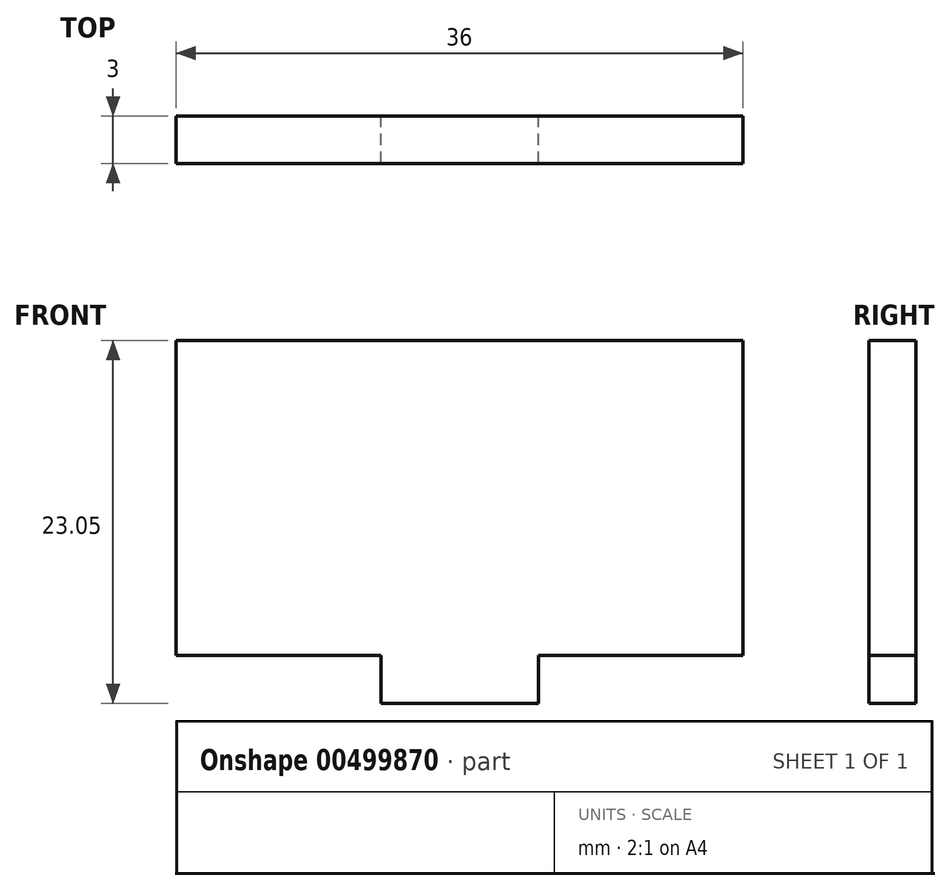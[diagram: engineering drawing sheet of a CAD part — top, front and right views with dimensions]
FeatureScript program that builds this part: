
annotation { "Feature Type Name" : "Feature", "Feature Type Description" : "" }
export const myFeature = defineFeature(function(context is Context, id is Id, definition is map)
    precondition{}
    {
        {
            var Q0;
            Q0=qCreatedBy(makeId("Front.planeOp"),FACE);
            var sketch = newSketch(context, id + "F0", { "sketchPlane" : qUnion([Q0])});
            skLineSegment(sketch, "E0.bottom", {"start": v(18, -10) * mm, "end": v(-18, -10) * mm});
            skLineSegment(sketch, "E0.top", {"start": v(18, 10) * mm, "end": v(-18, 10) * mm});
            skLineSegment(sketch, "E0.left", {"start": v(18, -10) * mm, "end": v(18, 10) * mm});
            skLineSegment(sketch, "E0.right", {"start": v(-18, -10) * mm, "end": v(-18, 10) * mm});
            skPoint(sketch, "E0.middle", {"position": v(0, 0) * mm});
            skLineSegment(sketch, "E1.bottom", {"start": v(5, -13.05) * mm, "end": v(-5, -13.05) * mm});
            skLineSegment(sketch, "E1.top", {"start": v(5, -10) * mm, "end": v(-5, -10) * mm});
            skLineSegment(sketch, "E1.left", {"start": v(5, -13.05) * mm, "end": v(5, -10) * mm});
            skLineSegment(sketch, "E1.right", {"start": v(-5, -13.05) * mm, "end": v(-5, -10) * mm});
            skPoint(sketch, "E1.middle", {"position": v(0, -11.52) * mm});
            skLineSegment(sketch, "E2.bottom", {"start": v(5, 10) * mm, "end": v(-5, 10) * mm});
            skLineSegment(sketch, "E2.top", {"start": v(5, 13.05) * mm, "end": v(-5, 13.05) * mm});
            skLineSegment(sketch, "E2.left", {"start": v(5, 10) * mm, "end": v(5, 13.05) * mm});
            skLineSegment(sketch, "E2.right", {"start": v(-5, 10) * mm, "end": v(-5, 13.05) * mm});
            skPoint(sketch, "E2.middle", {"position": v(0, 11.53) * mm});
            skSolve(sketch);
        }
        {
            var Q0;
            Q0=makeQuery(id+"F0.imprint","IMPRINT",FACE,{"disambiguationData":[TD([[makeQuery(id+"F0.imprint","IMPRINT",EDGE,{"derivedFrom":sQuery(id+"F0.wireOp",EDGE,"E2.bottom")}),-1.0]])]});
            var Q1;
            {var subQ3=sQuery(id+"F0.wireOp",EDGE,"E0.left");Q1=makeQuery(id+"F0.imprint","IMPRINT",FACE,{"disambiguationData":[TD([[makeQuery(id+"F0.imprint","IMPRINT",EDGE,{"derivedFrom":subQ3}),1.0]])]});}
            var Q2;
            Q2=makeQuery(id+"F0.imprint","IMPRINT",FACE,{"disambiguationData":[TD([[makeQuery(id+"F0.imprint","IMPRINT",EDGE,{"derivedFrom":sQuery(id+"F0.wireOp",EDGE,"E1.bottom")}),-1.0]])]});
            extrude(context, id + "F1", {"entities" : qUnion([Q0, Q1, Q2]), "depth" : 3 * mm, "offsetDistance" : 25 * mm});
        }
    });
